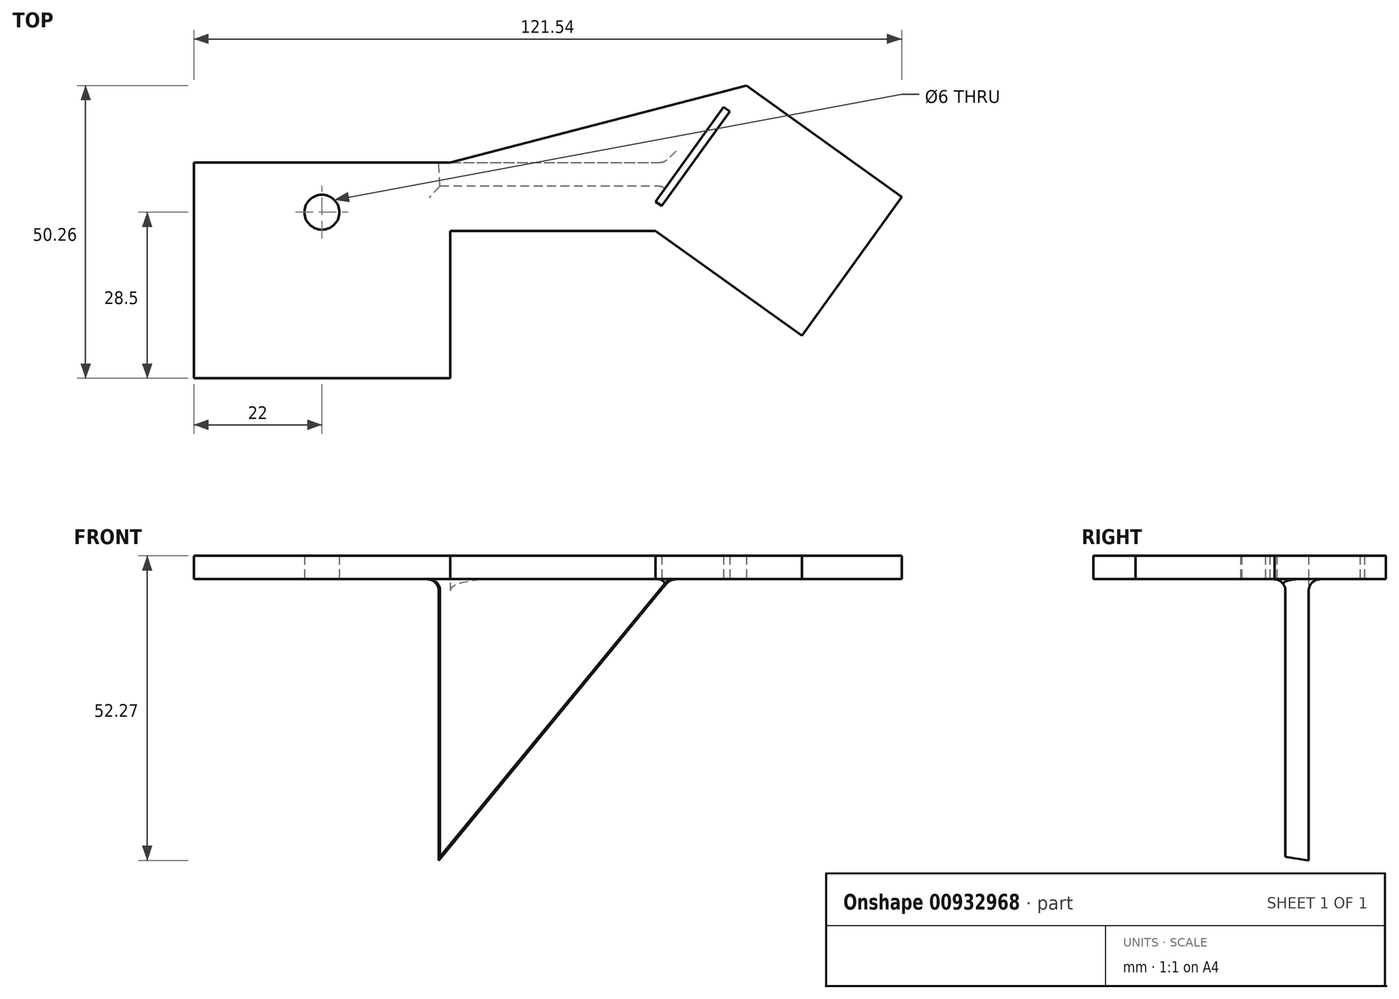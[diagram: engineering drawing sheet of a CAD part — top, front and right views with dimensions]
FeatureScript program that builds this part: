
annotation { "Feature Type Name" : "Feature", "Feature Type Description" : "" }
export const myFeature = defineFeature(function(context is Context, id is Id, definition is map)
    precondition{}
    {
        {
            var Q0;
            Q0=qCreatedBy(makeId("Top.planeOp"),FACE);
            var sketch = newSketch(context, id + "F0", { "sketchPlane" : qUnion([Q0])});
            skLineSegment(sketch, "E0", {"start": v(0, 0) * mm, "end": v(0, 37) * mm});
            skLineSegment(sketch, "E1", {"start": v(0, 37) * mm, "end": v(44, 37) * mm});
            skLineSegment(sketch, "E2", {"start": v(44, 25.3) * mm, "end": v(44, 0) * mm});
            skLineSegment(sketch, "E3", {"start": v(44, 0) * mm, "end": v(0, 0) * mm});
            skLineSegment(sketch, "E4", {"start": v(22, 37) * mm, "end": v(22, 28.5) * mm});
            skCircle(sketch, "E5", {"center": v(22, 28.5) * mm, "radius": 3 * mm});
            skLineSegment(sketch, "E6", {"start": v(44, 25.3) * mm, "end": v(79.3, 25.3) * mm});
            skLineSegment(sketch, "E7", {"start": v(79.3, 25.3) * mm, "end": v(104.42, 7.28) * mm});
            skLineSegment(sketch, "E8", {"start": v(104.42, 7.28) * mm, "end": v(121.54, 31.15) * mm});
            skLineSegment(sketch, "E9", {"start": v(121.54, 31.15) * mm, "end": v(94.9, 50.26) * mm});
            skLineSegment(sketch, "E10", {"start": v(94.9, 50.26) * mm, "end": v(44, 37) * mm});
            skLineSegment(sketch, "E11", {"start": v(90.99, 46.55) * mm, "end": v(79.3, 30.32) * mm});
            skLineSegment(sketch, "E12", {"start": v(90.99, 46.55) * mm, "end": v(92.03, 45.8) * mm});
            skLineSegment(sketch, "E13", {"start": v(92.03, 45.8) * mm, "end": v(80.34, 29.57) * mm});
            skLineSegment(sketch, "E14", {"start": v(80.34, 29.57) * mm, "end": v(79.3, 30.32) * mm});
            skSolve(sketch);
        }
        {
            var Q0;
            {var subQ0=sQuery(id+"F0.wireOp",EDGE,"E0");Q0=makeQuery(id+"F0.imprint","IMPRINT",FACE,{"disambiguationData":[TD([[makeQuery(id+"F0.imprint","IMPRINT",EDGE,{"derivedFrom":subQ0}),-1.0]])]});}
            extrude(context, id + "F1", {"entities" : qUnion([Q0]), "depth" : 4 * mm, "offsetDistance" : 25 * mm});
        }
        {
            var Q0;
            Q0=qCreatedBy(makeId("Front.planeOp"),FACE);
            var sketch = newSketch(context, id + "F2", { "sketchPlane" : qUnion([Q0])});
            skLineSegment(sketch, "E15", {"start": v(44, 0) * mm, "end": v(79.25, 0) * mm});
            skLineSegment(sketch, "E16", {"start": v(79.25, 0) * mm, "end": v(44, -42.86) * mm});
            skLineSegment(sketch, "E17", {"start": v(44, -42.86) * mm, "end": v(44, 0) * mm});
            skSolve(sketch);
        }
        {
            var Q0;
            Q0 = qSketchRegion(id + "F2", true);
            extrude(context, id + "F3", {"entities" : qUnion([Q0]), "operationType" : NewBodyOperationType.ADD, "oppositeDirection" : true, "depth" : 37 * mm, "offsetDistance" : 25 * mm, "hasDraft" : true, "draftAngle" : 3 * degree, "hasSecondDirection" : true, "secondDirectionOppositeDirection" : true, "secondDirectionDepth" : 33 * mm});
        }
        {
            var Q0;
            Q0=makeQuery(id+"F0.imprint","IMPRINT",FACE,{"disambiguationData":[TD([[makeQuery(id+"F0.imprint","IMPRINT",EDGE,{"derivedFrom":sQuery(id+"F0.wireOp",EDGE,"E11")}),1.0]])]});
            extrude(context, id + "F4", {"entities" : qUnion([Q0]), "operationType" : NewBodyOperationType.REMOVE, "endBound" : BoundingType.SYMMETRIC, "oppositeDirection" : true, "depth" : 25 * mm, "offsetDistance" : 25 * mm});
        }
        {
            var Q0;
            Q0=makeQuery(id+"F3.boolean.opBoolean","INTERSECT",EDGE,{"derivedFrom":[makeQuery(id+"F1.opExtrude","CAP_FACE",FACE,{"disambiguationData":[OSD([sQuery(id+"F0.wireOp",EDGE,"E0"),sQuery(id+"F0.wireOp",EDGE,"E1"),sQuery(id+"F0.wireOp",EDGE,"E2"),sQuery(id+"F0.wireOp",EDGE,"E3"),sQuery(id+"F0.wireOp",EDGE,"E5"),sQuery(id+"F0.wireOp",EDGE,"E6"),sQuery(id+"F0.wireOp",EDGE,"E7"),sQuery(id+"F0.wireOp",EDGE,"E8"),sQuery(id+"F0.wireOp",EDGE,"E9"),sQuery(id+"F0.wireOp",EDGE,"E10"),sQuery(id+"F0.wireOp",EDGE,"E11"),sQuery(id+"F0.wireOp",EDGE,"E12"),sQuery(id+"F0.wireOp",EDGE,"E13"),sQuery(id+"F0.wireOp",EDGE,"E14")])],"isStart":true}),makeQuery(id+"F3.opExtrude","SWEPT_FACE",FACE,{"disambiguationData":[OSD([sQuery(id+"F2.wireOp",EDGE,"E16")])]})]});
            var Q1;
            Q1=makeQuery(id+"F3.boolean.opBoolean","INTERSECT",EDGE,{"derivedFrom":[makeQuery(id+"F1.opExtrude","CAP_FACE",FACE,{"disambiguationData":[OSD([sQuery(id+"F0.wireOp",EDGE,"E0"),sQuery(id+"F0.wireOp",EDGE,"E1"),sQuery(id+"F0.wireOp",EDGE,"E2"),sQuery(id+"F0.wireOp",EDGE,"E3"),sQuery(id+"F0.wireOp",EDGE,"E5"),sQuery(id+"F0.wireOp",EDGE,"E6"),sQuery(id+"F0.wireOp",EDGE,"E7"),sQuery(id+"F0.wireOp",EDGE,"E8"),sQuery(id+"F0.wireOp",EDGE,"E9"),sQuery(id+"F0.wireOp",EDGE,"E10"),sQuery(id+"F0.wireOp",EDGE,"E11"),sQuery(id+"F0.wireOp",EDGE,"E12"),sQuery(id+"F0.wireOp",EDGE,"E13"),sQuery(id+"F0.wireOp",EDGE,"E14")])],"isStart":true}),makeQuery(id+"F3.opExtrude","CAP_FACE",FACE,{"disambiguationData":[OSD([sQuery(id+"F2.wireOp",EDGE,"E15"),sQuery(id+"F2.wireOp",EDGE,"E16"),sQuery(id+"F2.wireOp",EDGE,"E17")])],"isStart":false})]});
            var Q2;
            Q2=makeQuery(id+"F3.boolean.opBoolean","INTERSECT",EDGE,{"derivedFrom":[makeQuery(id+"F1.opExtrude","CAP_FACE",FACE,{"disambiguationData":[OSD([sQuery(id+"F0.wireOp",EDGE,"E0"),sQuery(id+"F0.wireOp",EDGE,"E1"),sQuery(id+"F0.wireOp",EDGE,"E2"),sQuery(id+"F0.wireOp",EDGE,"E3"),sQuery(id+"F0.wireOp",EDGE,"E5"),sQuery(id+"F0.wireOp",EDGE,"E6"),sQuery(id+"F0.wireOp",EDGE,"E7"),sQuery(id+"F0.wireOp",EDGE,"E8"),sQuery(id+"F0.wireOp",EDGE,"E9"),sQuery(id+"F0.wireOp",EDGE,"E10"),sQuery(id+"F0.wireOp",EDGE,"E11"),sQuery(id+"F0.wireOp",EDGE,"E12"),sQuery(id+"F0.wireOp",EDGE,"E13"),sQuery(id+"F0.wireOp",EDGE,"E14")])],"isStart":true}),makeQuery(id+"F3.opExtrude","CAP_FACE",FACE,{"disambiguationData":[OSD([sQuery(id+"F2.wireOp",EDGE,"E15"),sQuery(id+"F2.wireOp",EDGE,"E16"),sQuery(id+"F2.wireOp",EDGE,"E17")])],"isStart":true})]});
            var Q3;
            Q3=makeQuery(id+"F3.boolean.opBoolean","INTERSECT",EDGE,{"derivedFrom":[makeQuery(id+"F1.opExtrude","CAP_FACE",FACE,{"disambiguationData":[OSD([sQuery(id+"F0.wireOp",EDGE,"E0"),sQuery(id+"F0.wireOp",EDGE,"E1"),sQuery(id+"F0.wireOp",EDGE,"E2"),sQuery(id+"F0.wireOp",EDGE,"E3"),sQuery(id+"F0.wireOp",EDGE,"E5"),sQuery(id+"F0.wireOp",EDGE,"E6"),sQuery(id+"F0.wireOp",EDGE,"E7"),sQuery(id+"F0.wireOp",EDGE,"E8"),sQuery(id+"F0.wireOp",EDGE,"E9"),sQuery(id+"F0.wireOp",EDGE,"E10"),sQuery(id+"F0.wireOp",EDGE,"E11"),sQuery(id+"F0.wireOp",EDGE,"E12"),sQuery(id+"F0.wireOp",EDGE,"E13"),sQuery(id+"F0.wireOp",EDGE,"E14")])],"isStart":true}),makeQuery(id+"F3.opExtrude","SWEPT_FACE",FACE,{"disambiguationData":[OSD([sQuery(id+"F2.wireOp",EDGE,"E17")])]})]});
            fillet(context, id + "F5", {"entities" : qUnion([Q0, Q1, Q2, Q3]), "radius" : 2 * mm, "tangentPropagation" : true, "allowEdgeOverflow" : false});
        }
    });
